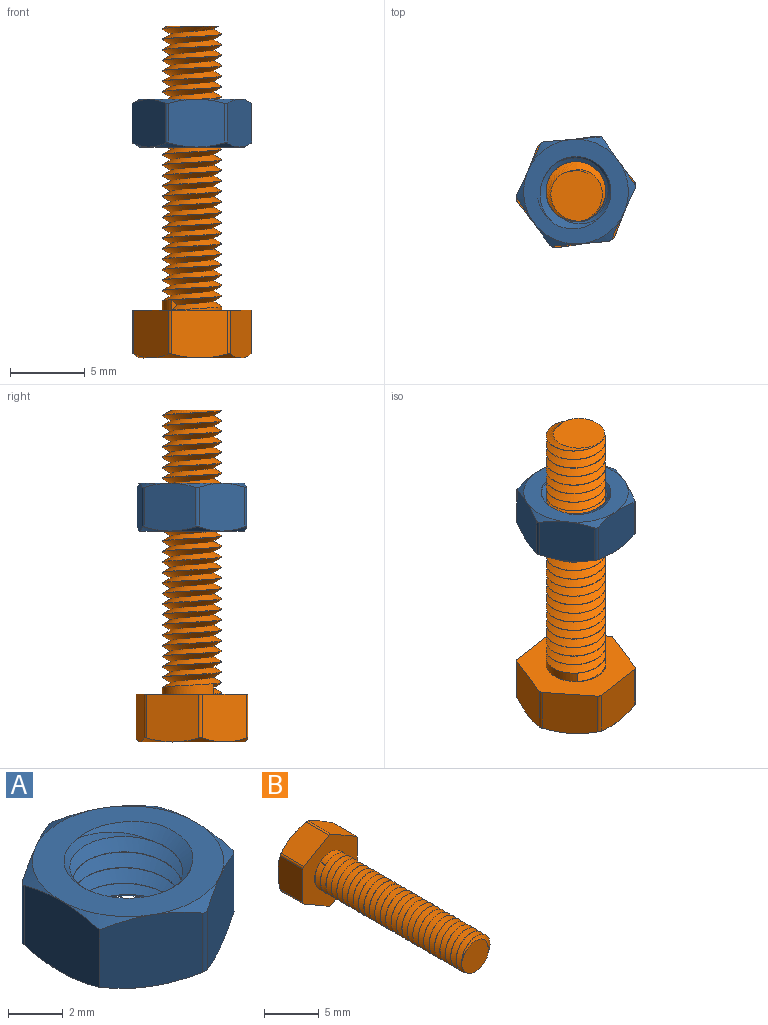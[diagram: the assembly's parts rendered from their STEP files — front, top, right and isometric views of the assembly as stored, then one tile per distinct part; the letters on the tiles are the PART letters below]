
ASSEMBLY  parts=2 mates=1
PART A: 30 faces, bbox 8.3x8.3x4.4 mm
  f0: plane 7.1x7.1mm, normal (0,0,1), area 20.5mm2, adj f5,f6,f8,f10,f12,f14,f21,f23
  f1: plane 7.12x7.12mm, normal (0,0,-1), area 20.5mm2, adj f3,f4,f7,f9,f11,f13,f22,f23
  f2: cylinder r=2mm len=4mm, axis (0,0,-1), area 1mm2, adj f21,f22,f23,f24
  f3: cone r=5.79mm half-angle=60deg, axis (0,0,1), area 1.2mm2, adj f1,f15,f16
  f4: cone r=5.79mm half-angle=60deg, axis (0,0,1), area 0.8mm2, adj f1,f15,f20,f29
  f5: cone r=5.79mm half-angle=60deg, axis (0,0,-1), area 1.2mm2, adj f0,f15,f16
  f6: cone r=5.79mm half-angle=60deg, axis (0,0,-1), area 0.8mm2, adj f0,f15,f20,f29
  f7: cone r=5.79mm half-angle=60deg, axis (0,0,1), area 0.8mm2, adj f1,f16,f17,f28
  f8: cone r=5.79mm half-angle=60deg, axis (0,0,-1), area 0.8mm2, adj f0,f16,f17,f28
  f9: cone r=5.79mm half-angle=60deg, axis (0,0,1), area 0.8mm2, adj f1,f17,f18,f27
  f10: cone r=5.79mm half-angle=60deg, axis (0,0,-1), area 0.8mm2, adj f0,f17,f18,f27
  f11: cone r=5.79mm half-angle=60deg, axis (0,0,1), area 0.8mm2, adj f1,f18,f19,f26
  f12: cone r=5.79mm half-angle=60deg, axis (0,0,-1), area 0.8mm2, adj f0,f18,f19,f26
  f13: cone r=5.79mm half-angle=60deg, axis (0,0,1), area 0.8mm2, adj f1,f19,f20,f25
  f14: cone r=5.79mm half-angle=60deg, axis (0,0,-1), area 0.8mm2, adj f0,f19,f20,f25
  f15: plane 3.71x3.54mm, normal (-0.5,-0.87,0), area 11.7mm2, adj f3,f4,f5,f6,f16,f29
  f16: plane 4.23x3.53mm, normal (-1,0,0), area 11.7mm2, adj f3,f5,f7,f8,f15,f28
  f17: plane 3.26x3.21mm, normal (-0.5,0.87,0), area 11.3mm2, adj f7,f8,f9,f10,f27,f28
  f18: plane 3.26x3.21mm, normal (0.5,0.87,0), area 11.3mm2, adj f9,f10,f11,f12,f26,f27
  f19: plane 3.76x3.2mm, normal (1,0,0), area 11.3mm2, adj f11,f12,f13,f14,f25,f26
  f20: plane 3.26x3.21mm, normal (0.5,-0.87,0), area 11.3mm2, adj f4,f6,f13,f14,f25,f29
  f21: cone r=2mm half-angle=45deg, axis (0,0,1), area 2mm2, adj f0,f2,f23,f24
  f22: cone r=2.34mm half-angle=45deg, axis (0,0,-1), area 2mm2, adj f1,f2,f23,f24
  f23: bspline ~5.99x5.19mm, area 42.8mm2, adj f0,f1,f2,f21,f22,f24
  f24: bspline ~5.99x5.19mm, area 42.8mm2, adj f0,f1,f2,f21,f22,f23
  f25: cylinder r=0.25mm len=2.66mm, axis (0,0,-1), area 0.7mm2, adj f13,f14,f19,f20
  f26: cylinder r=0.25mm len=2.66mm, axis (0,0,-1), area 0.7mm2, adj f11,f12,f18,f19
  f27: cylinder r=0.25mm len=2.66mm, axis (0,0,-1), area 0.7mm2, adj f9,f10,f17,f18
  f28: cylinder r=0.25mm len=2.66mm, axis (0,0,-1), area 0.7mm2, adj f7,f8,f16,f17
  f29: cylinder r=0.25mm len=2.66mm, axis (0,0,-1), area 0.7mm2, adj f4,f6,f15,f20
PART B: 25 faces, bbox 8.4x23.1x8.5 mm
  f0: cylinder r=2mm len=19mm, axis (0,1,0), area -72.6mm2, adj f7,f15,f16,f17,f18
  f1: plane 3.26x3.2mm, normal (0.5,0,-0.87), area 11.7mm2, adj f7,f9,f13,f19,f24
  f2: plane 3.76x3.2mm, normal (1,0,0), area 11.7mm2, adj f7,f12,f13,f19,f20
  f3: plane 3.26x3.2mm, normal (0.5,0,0.87), area 11.7mm2, adj f7,f11,f12,f20,f21
  f4: plane 3.26x3.2mm, normal (-0.5,0,0.87), area 11.7mm2, adj f7,f10,f11,f21,f22
  f5: plane 3.76x3.2mm, normal (-1,0,0), area 11.7mm2, adj f7,f8,f10,f22,f23
  f6: plane 3.26x3.2mm, normal (-0.5,0,-0.87), area 11.7mm2, adj f7,f8,f9,f23,f24
  f7: plane 8.01x7mm, normal (0,-1,0), area 29.8mm2, adj f0,f1,f2,f3,f4,f5,f6,f17
  f8: cone r=5.79mm half-angle=60deg, axis (0,-1,0), area 0.8mm2, adj f5,f6,f14,f23
  f9: cone r=5.79mm half-angle=60deg, axis (0,-1,0), area 0.8mm2, adj f1,f6,f14,f24
  f10: cone r=5.79mm half-angle=60deg, axis (0,-1,0), area 0.8mm2, adj f4,f5,f14,f22
  f11: cone r=5.79mm half-angle=60deg, axis (0,-1,0), area 0.8mm2, adj f3,f4,f14,f21
  f12: cone r=5.79mm half-angle=60deg, axis (0,-1,0), area 0.8mm2, adj f2,f3,f14,f20
  f13: cone r=5.79mm half-angle=60deg, axis (0,-1,0), area 0.8mm2, adj f1,f2,f14,f19
  f14: plane 7x7mm, normal (0,1,0), area 38.5mm2, adj f8,f9,f10,f11,f12,f13
  f15: plane 3.92x3.91mm, normal (0,-1,0), area 9.3mm2, adj f0,f17,f18
  f16: plane 0.69x0.47mm, normal (-0.78,0,-0.62), area 0.2mm2, adj f0,f17,f18
  f17: bspline ~19.36x4.62mm, area 196.1mm2, adj f0,f7,f15,f16,f18
  f18: bspline ~19.13x4.62mm, area 193.2mm2, adj f0,f15,f16,f17
  f19: cylinder r=0.25mm len=2.93mm, axis (0,1,0), area 0.8mm2, adj f1,f2,f7,f13
  f20: cylinder r=0.25mm len=2.93mm, axis (0,1,0), area 0.8mm2, adj f2,f3,f7,f12
  f21: cylinder r=0.25mm len=2.93mm, axis (0,1,0), area 0.8mm2, adj f3,f4,f7,f11
  f22: cylinder r=0.25mm len=2.93mm, axis (0,1,0), area 0.8mm2, adj f4,f5,f7,f10
  f23: cylinder r=0.25mm len=2.93mm, axis (0,1,0), area 0.8mm2, adj f5,f6,f7,f8
  f24: cylinder r=0.25mm len=2.93mm, axis (0,1,0), area 0.8mm2, adj f1,f6,f7,f9
PLACE A rot(axis=(0,0,-1),145deg) t=(23.4,-2.26,20.74)mm
PLACE B rot(axis=(-0.52,-0.6,0.6),124.9deg) t=(23.4,-2.26,6.64)mm
MATE cylindrical B.f0 <-> A.f3  axis (0,0,1) through (23.4,-2.26,28.84)mm
